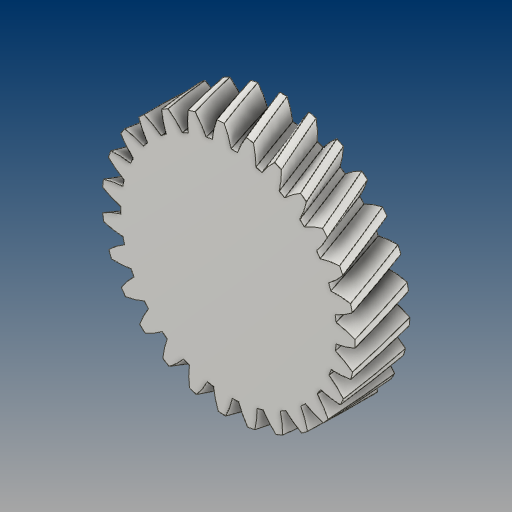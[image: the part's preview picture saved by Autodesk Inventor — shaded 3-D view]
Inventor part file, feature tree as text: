
AUTODESK INVENTOR PART (.ipt)
format: ipt  version: 2021 (Build 250183000, 183)  size: 533,504 bytes
history: native  units: mm (DEFAULTED — no unit token found)
features: plane x3, other x3, sketch x2, extrude x1
ambient origin geometry x8: Origin, YZ Plane, XZ Plane, XY Plane, X Axis, Y Axis, Z Axis, Center Point
bodies: Solid1 (feature_tree)
feature tree (9):
  extrude  "Extrusion1"  Depth=15.0mm TaperAngle=0.0deg
  plane  "Work Plane2"
  plane  "Work Plane8"
  plane  "Work Plane9"
  other  "Spur Gear"
  sketch  "Sketch1"  dims[d0=69.1488mm d1=15.0mm d2=0.0mm]
  sketch  "Sketch2"  dims[d3=64.6488mm d4=10.0mm d5=0.0mm d16=65.0mm d17=0.0mm d34=1.163553mm d39=0.0mm d41=0.0mm d43=65.0mm d46=65.0mm d47=0.0mm d48=0.0mm]
  other  "Srf1"
  other  "Pitch Diameter"
